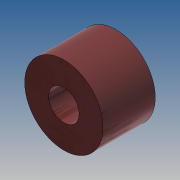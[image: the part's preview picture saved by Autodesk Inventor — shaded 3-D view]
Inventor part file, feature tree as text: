
AUTODESK INVENTOR PART (.ipt)
format: ipt  version: 2017 (Build 210142000, 142)  size: 88,064 bytes
history: native  units: mm
features: other x1, extrude x1, sketch x1
ambient origin geometry x8: Origin, YZ Plane, XZ Plane, XY Plane, X Axis, Y Axis, Z Axis, Center Point
bodies: Body1 (feature_tree)
feature tree (3):
  other  "Sólido1"
  extrude  "Extrusión1"  Depth=6.0mm
  sketch  "Boceto1"  dims[d0=3.5mm d1=8.0mm d2=6.0mm d3=0.0mm]
